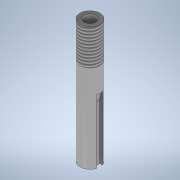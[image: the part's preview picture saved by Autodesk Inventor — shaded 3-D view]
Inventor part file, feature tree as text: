
AUTODESK INVENTOR PART (.ipt)
format: ipt  version: 2020 (Build 240168000, 168)  size: 138,752 bytes
history: native  units: in
note: dims shown in document units (in); Inventor stores cm internally (conversion verified against a paired STEP export)
features: extrude x3, sketch x3, thread x1, fillet x1
ambient origin geometry x8: Origin, YZ Plane, XZ Plane, XY Plane, X Axis, Y Axis, Z Axis, Center Point
bodies: Solid1 (feature_tree)
feature tree (8):
  extrude  "Extrusion1"  Depth=3.875in TaperAngle=0.0deg
  extrude  "Extrusion2"  Depth=2.0in TaperAngle=0.0deg
  thread  "Thread1"  [1 undecoded]
  extrude  "Extrusion3"  Depth=0.0938in
  fillet  "Fillet1"  Radius=2.0in
  sketch  "Sketch1"  dims[d0=0.624in d1=3.875in d2=0.0in]
  sketch  "Sketch2"  dims[d3=0.374in d4=2.0in d5=0.0in d6=1.125in d7=0.0in]
  sketch  "Sketch3"  dims[d8=0.0938in d9=0.0938in d10=2.0in d11=0.0in d12=0.4375in]
note: 1 required parameter value undecoded (feature->parameter linkage not recoverable at this tier; creation-order binding heuristic only, values carry confidence <= 0.55)
